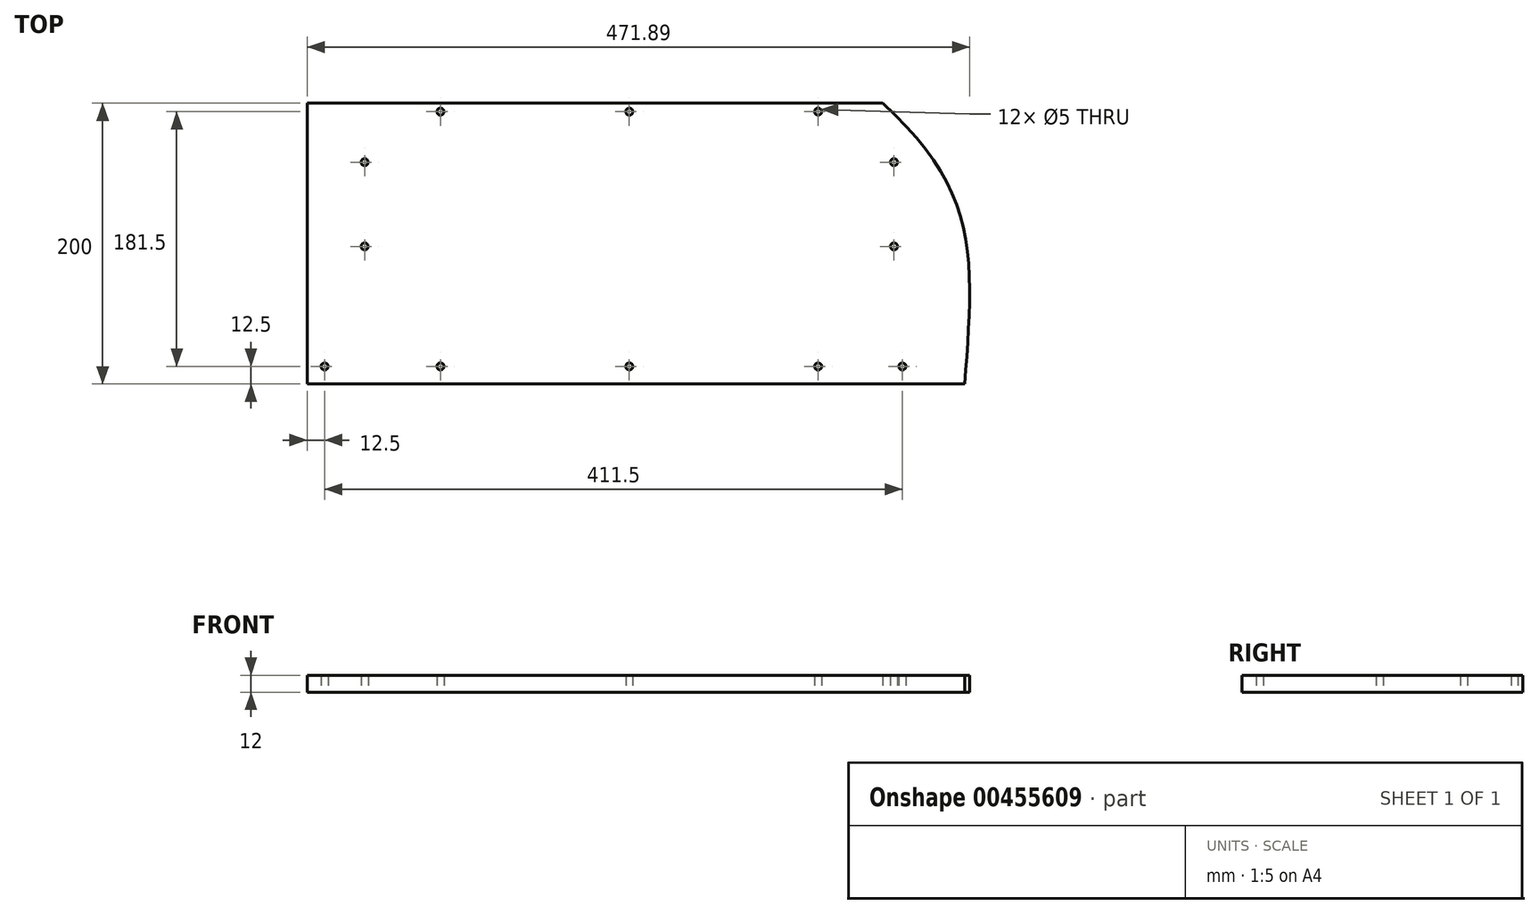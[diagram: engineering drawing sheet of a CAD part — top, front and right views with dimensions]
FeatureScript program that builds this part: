
annotation { "Feature Type Name" : "Feature", "Feature Type Description" : "" }
export const myFeature = defineFeature(function(context is Context, id is Id, definition is map)
    precondition{}
    {
        {
            var Q0;
            Q0=qCreatedBy(makeId("Top.planeOp"),FACE);
            var sketch = newSketch(context, id + "F0", { "sketchPlane" : qUnion([Q0])});
            skLineSegment(sketch, "E0.bottom", {"start": v(182.5, 81.5) * mm, "end": v(-182.5, 81.5) * mm, "construction": true});
            skLineSegment(sketch, "E0.top", {"start": v(240.74, -81.5) * mm, "end": v(-229.5, -81.5) * mm, "construction": true});
            skLineSegment(sketch, "E0.left", {"start": v(182.5, 81.5) * mm, "end": v(182.5, -81.35) * mm, "construction": true});
            skLineSegment(sketch, "E0.right", {"start": v(-182.5, 81.5) * mm, "end": v(-182.5, -81.5) * mm, "construction": true});
            skPoint(sketch, "E0.middle", {"position": v(0, 0) * mm});
            skLineSegment(sketch, "E1.0", {"start": v(194.5, -106.5) * mm, "end": v(-194.5, -106.5) * mm});
            skLineSegment(sketch, "E1.1", {"start": v(194.5, 93.5) * mm, "end": v(194.5, -106.5) * mm, "construction": true});
            skLineSegment(sketch, "E1.2", {"start": v(194.5, 93.5) * mm, "end": v(-194.5, 93.5) * mm});
            skLineSegment(sketch, "E1.3", {"start": v(-194.5, 93.5) * mm, "end": v(-194.5, -106.5) * mm, "construction": true});
            skLineSegment(sketch, "E2.0", {"start": v(188.5, 87.5) * mm, "end": v(-188.5, 87.5) * mm, "construction": true});
            skLineSegment(sketch, "E2.1", {"start": v(188.5, 87.5) * mm, "end": v(188.5, 85.91) * mm, "construction": true});
            skLineSegment(sketch, "E2.2", {"start": v(239.85, -94) * mm, "end": v(-229.5, -94) * mm, "construction": true});
            skLineSegment(sketch, "E2.3", {"start": v(-188.5, 87.5) * mm, "end": v(-188.5, -94) * mm, "construction": true});
            skCircle(sketch, "E3", {"center": v(-188.5, 51.5) * mm, "radius": 2.5 * mm});
            skCircle(sketch, "E4", {"center": v(-188.5, -8.5) * mm, "radius": 2.5 * mm});
            skCircle(sketch, "E5", {"center": v(188.5, -8.5) * mm, "radius": 2.5 * mm});
            skCircle(sketch, "E6", {"center": v(188.5, 51.5) * mm, "radius": 2.5 * mm});
            skCircle(sketch, "E7", {"center": v(0, 87.5) * mm, "radius": 2.5 * mm});
            skCircle(sketch, "E8", {"center": v(134.5, 87.5) * mm, "radius": 2.5 * mm});
            skCircle(sketch, "E9", {"center": v(-134.5, 87.5) * mm, "radius": 2.5 * mm});
            skCircle(sketch, "E10", {"center": v(0, -94) * mm, "radius": 2.5 * mm});
            skCircle(sketch, "E11", {"center": v(134.5, -94) * mm, "radius": 2.5 * mm});
            skCircle(sketch, "E12", {"center": v(-134.5, -94) * mm, "radius": 2.5 * mm});
            skLineSegment(sketch, "E13", {"start": v(-194.5, 93.5) * mm, "end": v(-229.5, 93.5) * mm});
            skLineSegment(sketch, "E14", {"start": v(-229.5, 93.5) * mm, "end": v(-229.5, -106.5) * mm});
            skLineSegment(sketch, "E15", {"start": v(-229.5, -106.5) * mm, "end": v(-194.5, -106.5) * mm});
            skLineSegment(sketch, "E16", {"start": v(194.5, -106.5) * mm, "end": v(238.93, -106.5) * mm});
            skLineSegment(sketch, "E17", {"start": v(180.5, 93.5) * mm, "end": v(194.5, 93.5) * mm});
            skFitSpline(sketch, "E18", {"points": [v(238.93, -106.5) * mm, v(238.93, 0) * mm, v(180.5, 93.5) * mm], "startDerivative": vector(16.47, 228.47) * mm, "endDerivative": vector(-212.92, 195.64) * mm});
            skLineSegment(sketch, "E19", {"start": v(-204.5, 93.5) * mm, "end": v(-204.5, -106.5) * mm, "construction": true});
            skPoint(sketch, "E20.orphan", {"position": v(182.5, -81.5) * mm});
            skCircle(sketch, "E21", {"center": v(194.5, -94) * mm, "radius": 2.5 * mm});
            skCircle(sketch, "E22", {"center": v(-217, -94) * mm, "radius": 2.5 * mm});
            skSolve(sketch);
        }
        {
            var Q0;
            Q0 = qSketchRegion(id + "F0", true);
            extrude(context, id + "F1", {"entities" : qUnion([Q0]), "depth" : 12 * mm});
        }
    });
